# Revit family: SC_ZTubest
name_source: partatom
category: Structural Columns
units: mm (PartAtom-declared; Revit-internal decimal feet)

## family parameters
Always export as geometry = No
Beam cutback in plan = From bounding box
Cut with Voids When Loaded = No
Material for Model Behavior = Steel
Section Shape = Not Defined
Shared = No
Show family pre-cut in plan views = Yes

## types (24) — shared parameters
R = 3 mm

## per-type parameters (varying)
| type | A | Bi | Bs | C | e |
| Z 250x75x20x3 | 250 mm | 70 mm | 75 mm | 20 mm | 3 mm |
| Z 250x75x20x2.5 | 250 mm | 70 mm | 75 mm | 20 mm | 3 mm |
| Z 250x75x20x2 | 250 mm | 70 mm | 75 mm | 20 mm | 2 mm |
| Z 250x75x20x1.6 | 250 mm | 70 mm | 75 mm | 20 mm | 2 mm |
| Z 200x75x20x3 | 200 mm | 70 mm | 75 mm | 20 mm | 3 mm |
| Z 200x75x20x2.5 | 200 mm | 70 mm | 75 mm | 20 mm | 3 mm |
| Z 200x75x20x2 | 200 mm | 70 mm | 75 mm | 20 mm | 2 mm |
| Z 200x75x20x1.6 | 200 mm | 70 mm | 75 mm | 20 mm | 2 mm |
| Z 175x75x20x3 | 175 mm | 70 mm | 75 mm | 20 mm | 3 mm |
| Z 175x75x20x2.5 | 175 mm | 70 mm | 75 mm | 20 mm | 3 mm |
| Z 175x75x20x2 | 175 mm | 70 mm | 75 mm | 20 mm | 2 mm |
| Z 175x75x20x1.6 | 175 mm | 70 mm | 75 mm | 20 mm | 2 mm |
| Z 150x50x15x3 | 150 mm | 45 mm | 50 mm | 15 mm | 3 mm |
| Z 150x50x15x2.5 | 150 mm | 45 mm | 50 mm | 15 mm | 3 mm |
| Z 150x50x15x2 | 150 mm | 45 mm | 50 mm | 15 mm | 2 mm |
| Z 150x50x15x1.6 | 150 mm | 45 mm | 50 mm | 15 mm | 2 mm |
| Z 125x50x15x3 | 125 mm | 45 mm | 50 mm | 15 mm | 3 mm |
| Z 125x50x15x2.5 | 125 mm | 45 mm | 50 mm | 15 mm | 3 mm |
| Z 125x50x15x2 | 125 mm | 45 mm | 50 mm | 15 mm | 2 mm |
| Z 125x50x15x1.6 | 125 mm | 45 mm | 50 mm | 15 mm | 2 mm |
| Z 100x50x15x3 | 100 mm | 45 mm | 50 mm | 15 mm | 3 mm |
| Z 100x50x15x2.5 | 100 mm | 45 mm | 50 mm | 15 mm | 3 mm |
| Z 100x50x15x2 | 100 mm | 45 mm | 50 mm | 15 mm | 2 mm |
| Z 100x50x15x1.6 | 100 mm | 45 mm | 50 mm | 15 mm | 2 mm |

## geometry (parser evidence)
native form markers: Blend x2, Sweep x2
no freeform markers — native parametric forms only
